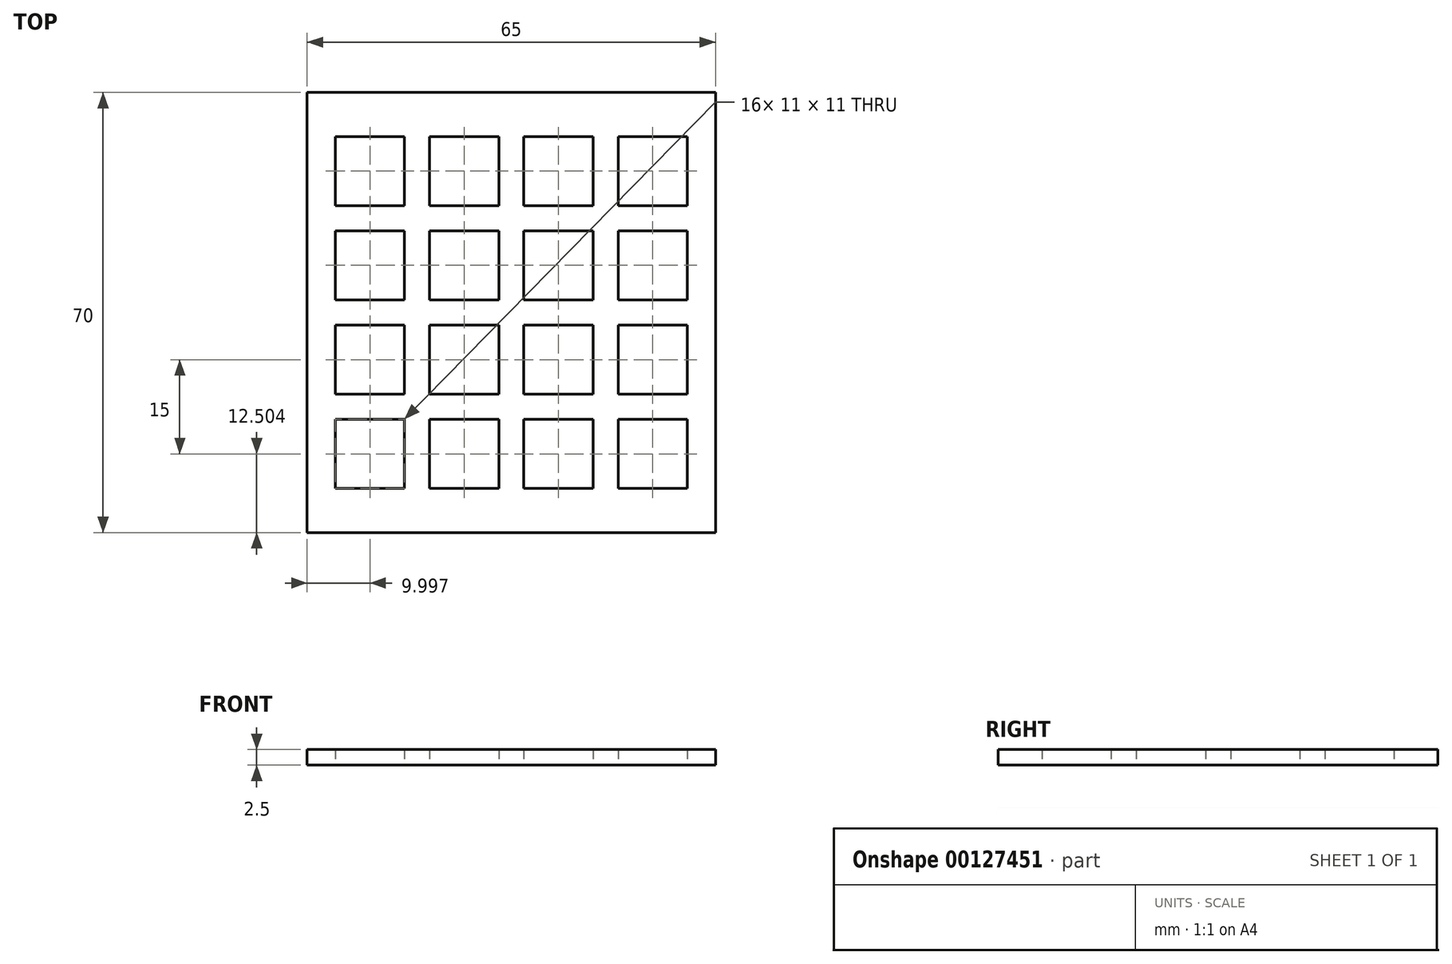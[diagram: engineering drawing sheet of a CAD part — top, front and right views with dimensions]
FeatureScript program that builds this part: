
annotation { "Feature Type Name" : "Feature", "Feature Type Description" : "" }
export const myFeature = defineFeature(function(context is Context, id is Id, definition is map)
    precondition{}
    {
        {
            var Q0;
            Q0=qCreatedBy(makeId("Top.planeOp"),FACE);
            var sketch = newSketch(context, id + "F0", { "sketchPlane" : qUnion([Q0])});
            skLineSegment(sketch, "E0.bottom", {"start": v(-44.9, 34.57) * mm, "end": v(20.1, 34.57) * mm});
            skLineSegment(sketch, "E0.top", {"start": v(-44.9, -39.43) * mm, "end": v(20.1, -39.43) * mm});
            skLineSegment(sketch, "E0.left", {"start": v(-44.9, 34.57) * mm, "end": v(-44.9, -39.43) * mm});
            skLineSegment(sketch, "E0.right", {"start": v(20.1, 34.57) * mm, "end": v(20.1, -39.43) * mm});
            skLineSegment(sketch, "E1", {"start": v(-44.9, 34.57) * mm, "end": v(-40.4, 34.57) * mm, "construction": true});
            skLineSegment(sketch, "E2", {"start": v(-40.4, 34.57) * mm, "end": v(-29.4, 34.57) * mm, "construction": true});
            skLineSegment(sketch, "E3", {"start": v(-29.4, 34.57) * mm, "end": v(-25.4, 34.57) * mm, "construction": true});
            skLineSegment(sketch, "E4", {"start": v(-25.4, 34.57) * mm, "end": v(-14.4, 34.57) * mm, "construction": true});
            skLineSegment(sketch, "E5", {"start": v(-14.4, 34.57) * mm, "end": v(-10.4, 34.57) * mm, "construction": true});
            skLineSegment(sketch, "E6", {"start": v(-10.4, 34.57) * mm, "end": v(0.6, 34.57) * mm, "construction": true});
            skLineSegment(sketch, "E7", {"start": v(0.6, 34.57) * mm, "end": v(4.6, 34.57) * mm, "construction": true});
            skLineSegment(sketch, "E8", {"start": v(4.6, 34.57) * mm, "end": v(15.6, 34.57) * mm, "construction": true});
            skLineSegment(sketch, "E9", {"start": v(15.6, 34.57) * mm, "end": v(20.1, 34.57) * mm, "construction": true});
            skLineSegment(sketch, "E10", {"start": v(-44.9, 34.57) * mm, "end": v(-44.9, 27.57) * mm, "construction": true});
            skLineSegment(sketch, "E11", {"start": v(-44.9, 27.57) * mm, "end": v(-44.9, 16.57) * mm, "construction": true});
            skLineSegment(sketch, "E12", {"start": v(-44.9, 16.57) * mm, "end": v(-44.9, 12.57) * mm, "construction": true});
            skLineSegment(sketch, "E13", {"start": v(-44.9, 12.57) * mm, "end": v(-44.9, 1.57) * mm, "construction": true});
            skLineSegment(sketch, "E14", {"start": v(-44.9, 1.57) * mm, "end": v(-44.9, -2.43) * mm, "construction": true});
            skLineSegment(sketch, "E15", {"start": v(-44.9, -2.43) * mm, "end": v(-44.9, -13.43) * mm, "construction": true});
            skLineSegment(sketch, "E16", {"start": v(-44.9, -13.43) * mm, "end": v(-44.9, -17.43) * mm, "construction": true});
            skLineSegment(sketch, "E17", {"start": v(-44.9, -17.43) * mm, "end": v(-44.9, -28.43) * mm, "construction": true});
            skLineSegment(sketch, "E18", {"start": v(-44.9, -28.43) * mm, "end": v(-44.9, -35.43) * mm, "construction": true});
            skLineSegment(sketch, "E19", {"start": v(-44.9, -35.43) * mm, "end": v(20.1, -35.43) * mm});
            skLineSegment(sketch, "E20", {"start": v(20.1, -35.43) * mm, "end": v(20.1, 34.57) * mm});
            skLineSegment(sketch, "E21.bottom", {"start": v(-40.4, 27.57) * mm, "end": v(-29.4, 27.57) * mm});
            skLineSegment(sketch, "E21.top", {"start": v(-40.4, 16.57) * mm, "end": v(-29.4, 16.57) * mm});
            skLineSegment(sketch, "E21.left", {"start": v(-40.4, 27.57) * mm, "end": v(-40.4, 16.57) * mm});
            skLineSegment(sketch, "E21.right", {"start": v(-29.4, 27.57) * mm, "end": v(-29.4, 16.57) * mm});
            skLineSegment(sketch, "E22.bottom", {"start": v(-25.4, 27.57) * mm, "end": v(-14.4, 27.57) * mm});
            skLineSegment(sketch, "E22.top", {"start": v(-25.4, 16.57) * mm, "end": v(-14.4, 16.57) * mm});
            skLineSegment(sketch, "E22.left", {"start": v(-25.4, 27.57) * mm, "end": v(-25.4, 16.57) * mm});
            skLineSegment(sketch, "E22.right", {"start": v(-14.4, 27.57) * mm, "end": v(-14.4, 16.57) * mm});
            skLineSegment(sketch, "E23.bottom", {"start": v(-10.4, 27.57) * mm, "end": v(0.6, 27.57) * mm});
            skLineSegment(sketch, "E23.top", {"start": v(-10.4, 16.57) * mm, "end": v(0.6, 16.57) * mm});
            skLineSegment(sketch, "E23.left", {"start": v(-10.4, 27.57) * mm, "end": v(-10.4, 16.57) * mm});
            skLineSegment(sketch, "E23.right", {"start": v(0.6, 27.57) * mm, "end": v(0.6, 16.57) * mm});
            skLineSegment(sketch, "E24.bottom", {"start": v(4.6, 27.57) * mm, "end": v(15.6, 27.57) * mm});
            skLineSegment(sketch, "E24.top", {"start": v(4.6, 16.57) * mm, "end": v(15.6, 16.57) * mm});
            skLineSegment(sketch, "E24.left", {"start": v(4.6, 27.57) * mm, "end": v(4.6, 16.57) * mm});
            skLineSegment(sketch, "E24.right", {"start": v(15.6, 27.57) * mm, "end": v(15.6, 16.57) * mm});
            skLineSegment(sketch, "E25.bottom", {"start": v(-40.4, 12.57) * mm, "end": v(-29.4, 12.57) * mm});
            skLineSegment(sketch, "E25.top", {"start": v(-40.4, 1.57) * mm, "end": v(-29.4, 1.57) * mm});
            skLineSegment(sketch, "E25.left", {"start": v(-40.4, 12.57) * mm, "end": v(-40.4, 1.57) * mm});
            skLineSegment(sketch, "E25.right", {"start": v(-29.4, 12.57) * mm, "end": v(-29.4, 1.57) * mm});
            skLineSegment(sketch, "E26.bottom", {"start": v(-25.4, 12.57) * mm, "end": v(-14.4, 12.57) * mm});
            skLineSegment(sketch, "E26.top", {"start": v(-25.4, 1.57) * mm, "end": v(-14.4, 1.57) * mm});
            skLineSegment(sketch, "E26.left", {"start": v(-25.4, 12.57) * mm, "end": v(-25.4, 1.57) * mm});
            skLineSegment(sketch, "E26.right", {"start": v(-14.4, 12.57) * mm, "end": v(-14.4, 1.57) * mm});
            skLineSegment(sketch, "E27.bottom", {"start": v(-10.4, 12.57) * mm, "end": v(0.6, 12.57) * mm});
            skLineSegment(sketch, "E27.top", {"start": v(-10.4, 1.57) * mm, "end": v(0.6, 1.57) * mm});
            skLineSegment(sketch, "E27.left", {"start": v(-10.4, 12.57) * mm, "end": v(-10.4, 1.57) * mm});
            skLineSegment(sketch, "E27.right", {"start": v(0.6, 12.57) * mm, "end": v(0.6, 1.57) * mm});
            skLineSegment(sketch, "E28.bottom", {"start": v(4.6, 12.57) * mm, "end": v(15.6, 12.57) * mm});
            skLineSegment(sketch, "E28.top", {"start": v(4.6, 1.57) * mm, "end": v(15.6, 1.57) * mm});
            skLineSegment(sketch, "E28.left", {"start": v(4.6, 12.57) * mm, "end": v(4.6, 1.57) * mm});
            skLineSegment(sketch, "E28.right", {"start": v(15.6, 12.57) * mm, "end": v(15.6, 1.57) * mm});
            skLineSegment(sketch, "E29.bottom", {"start": v(-40.4, -2.43) * mm, "end": v(-29.4, -2.43) * mm});
            skLineSegment(sketch, "E29.top", {"start": v(-40.4, -13.43) * mm, "end": v(-29.4, -13.43) * mm});
            skLineSegment(sketch, "E29.left", {"start": v(-40.4, -2.43) * mm, "end": v(-40.4, -13.43) * mm});
            skLineSegment(sketch, "E29.right", {"start": v(-29.4, -2.43) * mm, "end": v(-29.4, -13.43) * mm});
            skLineSegment(sketch, "E30.bottom", {"start": v(-25.4, -2.43) * mm, "end": v(-14.4, -2.43) * mm});
            skLineSegment(sketch, "E30.top", {"start": v(-25.4, -13.43) * mm, "end": v(-14.4, -13.43) * mm});
            skLineSegment(sketch, "E30.left", {"start": v(-25.4, -2.43) * mm, "end": v(-25.4, -13.43) * mm});
            skLineSegment(sketch, "E30.right", {"start": v(-14.4, -2.43) * mm, "end": v(-14.4, -13.43) * mm});
            skLineSegment(sketch, "E31.bottom", {"start": v(-10.4, -2.43) * mm, "end": v(0.6, -2.43) * mm});
            skLineSegment(sketch, "E31.top", {"start": v(-10.4, -13.43) * mm, "end": v(0.6, -13.43) * mm});
            skLineSegment(sketch, "E31.left", {"start": v(-10.4, -2.43) * mm, "end": v(-10.4, -13.43) * mm});
            skLineSegment(sketch, "E31.right", {"start": v(0.6, -2.43) * mm, "end": v(0.6, -13.43) * mm});
            skLineSegment(sketch, "E32.bottom", {"start": v(4.6, -2.43) * mm, "end": v(15.6, -2.43) * mm});
            skLineSegment(sketch, "E32.top", {"start": v(4.6, -13.43) * mm, "end": v(15.6, -13.43) * mm});
            skLineSegment(sketch, "E32.left", {"start": v(4.6, -2.43) * mm, "end": v(4.6, -13.43) * mm});
            skLineSegment(sketch, "E32.right", {"start": v(15.6, -2.43) * mm, "end": v(15.6, -13.43) * mm});
            skLineSegment(sketch, "E33.bottom", {"start": v(-40.4, -17.43) * mm, "end": v(-29.4, -17.43) * mm});
            skLineSegment(sketch, "E33.top", {"start": v(-40.4, -28.43) * mm, "end": v(-29.4, -28.43) * mm});
            skLineSegment(sketch, "E33.left", {"start": v(-40.4, -17.43) * mm, "end": v(-40.4, -28.43) * mm});
            skLineSegment(sketch, "E33.right", {"start": v(-29.4, -17.43) * mm, "end": v(-29.4, -28.43) * mm});
            skLineSegment(sketch, "E34.bottom", {"start": v(-25.4, -17.43) * mm, "end": v(-14.4, -17.43) * mm});
            skLineSegment(sketch, "E34.top", {"start": v(-25.4, -28.43) * mm, "end": v(-14.4, -28.43) * mm});
            skLineSegment(sketch, "E34.left", {"start": v(-25.4, -17.43) * mm, "end": v(-25.4, -28.43) * mm});
            skLineSegment(sketch, "E34.right", {"start": v(-14.4, -17.43) * mm, "end": v(-14.4, -28.43) * mm});
            skLineSegment(sketch, "E35.bottom", {"start": v(-10.4, -17.43) * mm, "end": v(0.6, -17.43) * mm});
            skLineSegment(sketch, "E35.top", {"start": v(-10.4, -28.43) * mm, "end": v(0.6, -28.43) * mm});
            skLineSegment(sketch, "E35.left", {"start": v(-10.4, -17.43) * mm, "end": v(-10.4, -28.43) * mm});
            skLineSegment(sketch, "E35.right", {"start": v(0.6, -17.43) * mm, "end": v(0.6, -28.43) * mm});
            skLineSegment(sketch, "E36.bottom", {"start": v(4.6, -17.43) * mm, "end": v(15.6, -17.43) * mm});
            skLineSegment(sketch, "E36.top", {"start": v(4.6, -28.43) * mm, "end": v(15.6, -28.43) * mm});
            skLineSegment(sketch, "E36.left", {"start": v(4.6, -17.43) * mm, "end": v(4.6, -28.43) * mm});
            skLineSegment(sketch, "E36.right", {"start": v(15.6, -17.43) * mm, "end": v(15.6, -28.43) * mm});
            skSolve(sketch);
        }
        {
            var Q0;
            {var subQ1=sQuery(id+"F0.wireOp",EDGE,"E0.bottom");Q0=makeQuery(id+"F0.imprint","IMPRINT",FACE,{"disambiguationData":[TD([[makeQuery(id+"F0.imprint","IMPRINT",EDGE,{"derivedFrom":subQ1}),-1.0]])]});}
            extrude(context, id + "F1", {"entities" : qUnion([Q0]), "depth" : 2.5 * mm});
        }
    });
